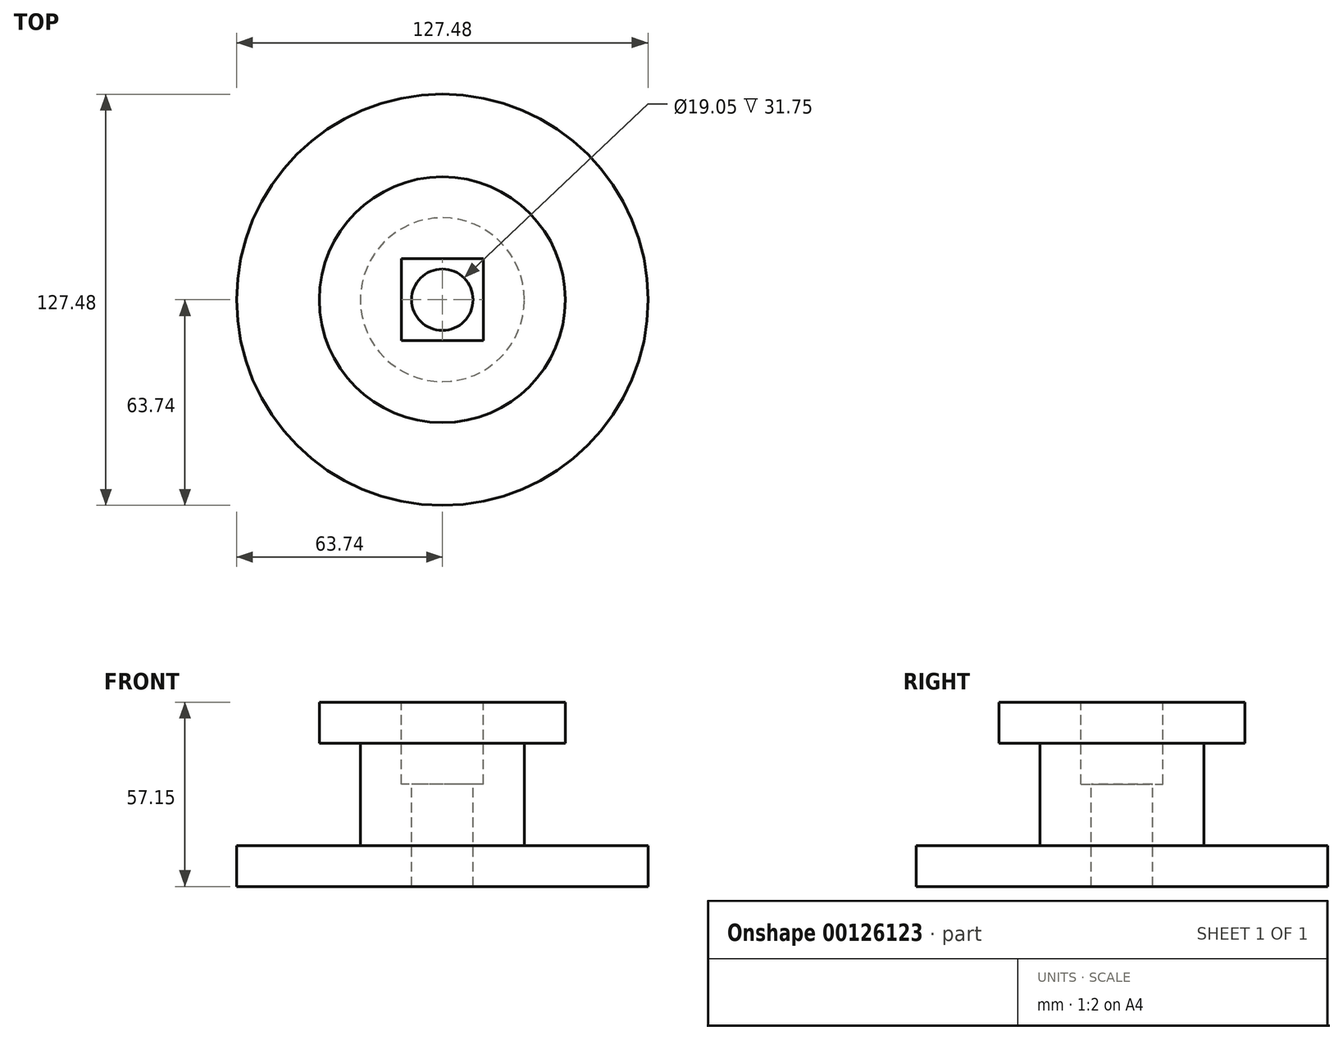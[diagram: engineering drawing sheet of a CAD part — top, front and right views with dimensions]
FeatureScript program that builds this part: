
annotation { "Feature Type Name" : "Feature", "Feature Type Description" : "" }
export const myFeature = defineFeature(function(context is Context, id is Id, definition is map)
    precondition{}
    {
        {
            var Q0;
            Q0=qCreatedBy(makeId("Top.planeOp"),FACE);
            var sketch = newSketch(context, id + "F0", { "sketchPlane" : qUnion([Q0])});
            skCircle(sketch, "E0", {"center": v(0, 0) * mm, "radius": 63.74 * mm});
            skSolve(sketch);
        }
        {
            var Q0;
            Q0=makeQuery(id+"F0.imprint","IMPRINT",FACE,{"disambiguationData":[TD([[makeQuery(id+"F0.imprint","IMPRINT",EDGE,{"derivedFrom":sQuery(id+"F0.wireOp",EDGE,"E0")}),1.0]])]});
            extrude(context, id + "F1", {"entities" : qUnion([Q0]), "depth" : 12.7 * mm});
        }
        {
            var Q0;
            Q0=makeQuery(id+"F1.opExtrude","CAP_FACE",FACE,{"disambiguationData":[OSD([sQuery(id+"F0.wireOp",EDGE,"E0")])],"isStart":false});
            var sketch = newSketch(context, id + "F2", { "sketchPlane" : qUnion([Q0])});
            skCircle(sketch, "E1", {"center": v(0, 0) * mm, "radius": 25.4 * mm});
            skSolve(sketch);
        }
        {
            var Q0;
            Q0 = qSketchRegion(id + "F2", true);
            extrude(context, id + "F3", {"entities" : qUnion([Q0]), "operationType" : NewBodyOperationType.ADD, "depth" : 19.05 * mm});
        }
        {
            var Q0;
            Q0=makeQuery(id+"F3.opExtrude","CAP_FACE",FACE,{"disambiguationData":[OSD([sQuery(id+"F2.wireOp",EDGE,"E1")])],"isStart":false});
            var sketch = newSketch(context, id + "F4", { "sketchPlane" : qUnion([Q0])});
            skCircle(sketch, "E2", {"center": v(0, 0) * mm, "radius": 9.53 * mm});
            skSolve(sketch);
        }
        {
            var Q0;
            Q0 = qSketchRegion(id + "F4", true);
            extrude(context, id + "F5", {"entities" : qUnion([Q0]), "operationType" : NewBodyOperationType.REMOVE, "oppositeDirection" : true, "depth" : 50.8 * mm});
        }
        {
            var Q0;
            Q0=makeQuery(id+"F3.opExtrude","CAP_FACE",FACE,{"disambiguationData":[OSD([sQuery(id+"F2.wireOp",EDGE,"E1")])],"isStart":false});
            extrude(context, id + "F6", {"entities" : qUnion([Q0]), "operationType" : NewBodyOperationType.ADD, "depth" : 12.7 * mm});
        }
        {
            var Q0;
            Q0=makeQuery(id+"F6.opExtrude","CAP_FACE",FACE,{"disambiguationData":[OSD([sQuery(id+"F2.wireOp",EDGE,"E1")])],"isStart":false});
            var sketch = newSketch(context, id + "F7", { "sketchPlane" : qUnion([Q0])});
            skCircle(sketch, "E3", {"center": v(0, 0) * mm, "radius": 38.1 * mm});
            skSolve(sketch);
        }
        {
            var Q0;
            Q0 = qSketchRegion(id + "F7", true);
            extrude(context, id + "F8", {"entities" : qUnion([Q0]), "operationType" : NewBodyOperationType.ADD, "depth" : 12.7 * mm});
        }
        {
            var Q0;
            Q0=makeQuery(id+"F8.opExtrude","CAP_FACE",FACE,{"disambiguationData":[OSD([sQuery(id+"F7.wireOp",EDGE,"E3")])],"isStart":false});
            var sketch = newSketch(context, id + "F9", { "sketchPlane" : qUnion([Q0])});
            skLineSegment(sketch, "E4.bottom", {"start": v(12.7, -12.7) * mm, "end": v(-12.7, -12.7) * mm});
            skLineSegment(sketch, "E4.top", {"start": v(12.7, 12.7) * mm, "end": v(-12.7, 12.7) * mm});
            skLineSegment(sketch, "E4.left", {"start": v(12.7, -12.7) * mm, "end": v(12.7, 12.7) * mm});
            skLineSegment(sketch, "E4.right", {"start": v(-12.7, -12.7) * mm, "end": v(-12.7, 12.7) * mm});
            skPoint(sketch, "E4.middle", {"position": v(0, 0) * mm});
            skSolve(sketch);
        }
        {
            var Q0;
            Q0 = qSketchRegion(id + "F9", true);
            extrude(context, id + "F10", {"entities" : qUnion([Q0]), "operationType" : NewBodyOperationType.REMOVE, "oppositeDirection" : true, "depth" : 25.4 * mm});
        }
    });
